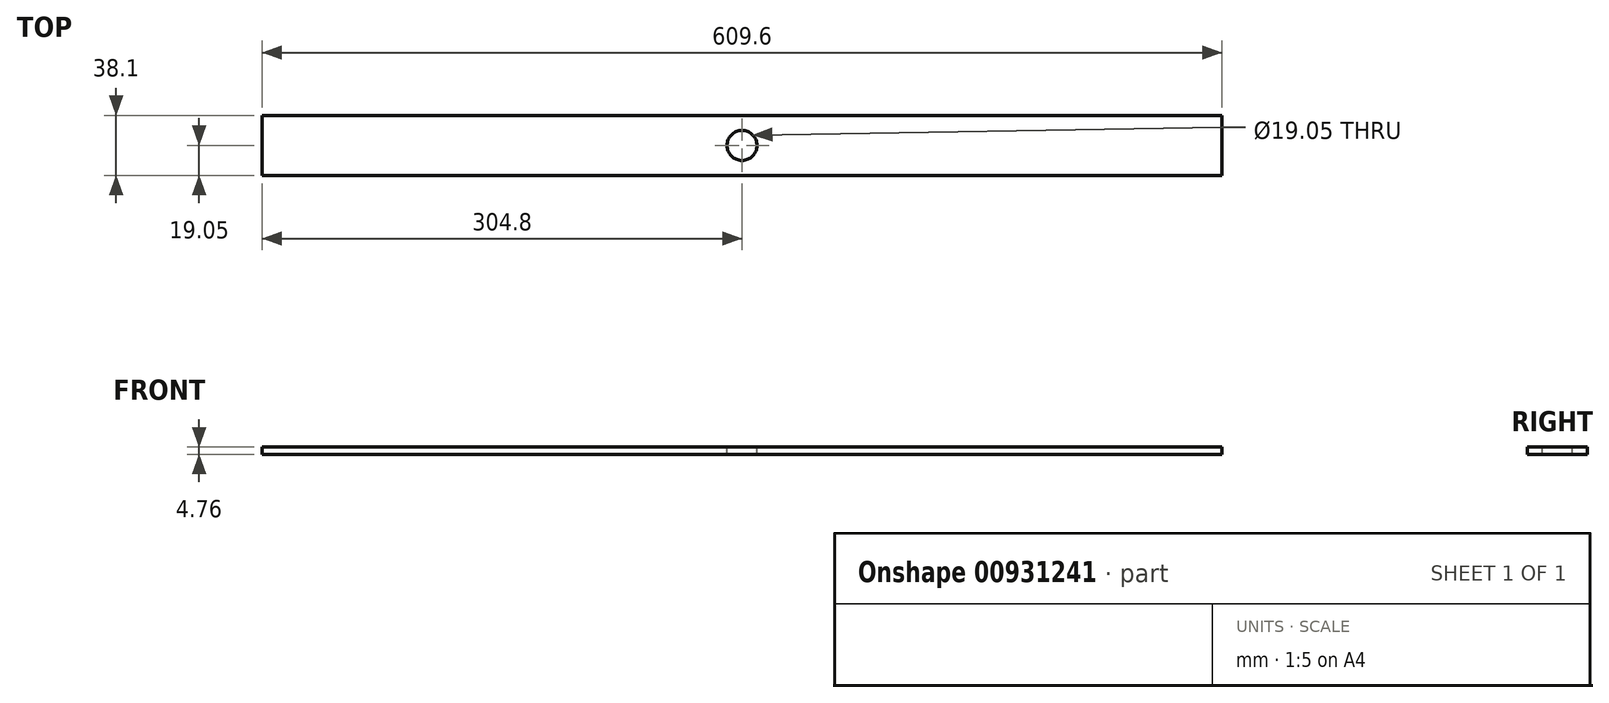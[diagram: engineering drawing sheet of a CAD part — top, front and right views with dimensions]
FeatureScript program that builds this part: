
annotation { "Feature Type Name" : "Feature", "Feature Type Description" : "" }
export const myFeature = defineFeature(function(context is Context, id is Id, definition is map)
    precondition{}
    {
        {
            var Q0;
            Q0=qCreatedBy(makeId("Right.planeOp"),FACE);
            var sketch = newSketch(context, id + "F0", { "sketchPlane" : qUnion([Q0])});
            skLineSegment(sketch, "E0.bottom", {"start": v(0, 0) * mm, "end": v(38.1, 0) * mm});
            skLineSegment(sketch, "E0.top", {"start": v(0, 4.76) * mm, "end": v(38.1, 4.76) * mm});
            skLineSegment(sketch, "E0.left", {"start": v(0, 0) * mm, "end": v(0, 4.76) * mm});
            skLineSegment(sketch, "E0.right", {"start": v(38.1, 0) * mm, "end": v(38.1, 4.76) * mm});
            skSolve(sketch);
        }
        {
            var Q0;
            Q0 = qSketchRegion(id + "F0", true);
            extrude(context, id + "F1", {"entities" : qUnion([Q0]), "depth" : 609.6 * mm, "offsetDistance" : 25.4 * mm});
        }
        {
            var Q0;
            Q0=makeQuery(id+"F1.opExtrude","SWEPT_FACE",FACE,{"disambiguationData":[OSD([sQuery(id+"F0.wireOp",EDGE,"E0.top")])]});
            var sketch = newSketch(context, id + "F2", { "sketchPlane" : qUnion([Q0])});
            skCircle(sketch, "E1", {"center": v(304.8, 19.05) * mm, "radius": 9.53 * mm});
            skPoint(sketch, "E1.centerSnap0", {"position": v(304.8, 38.1) * mm});
            skPoint(sketch, "E1.centerSnap1", {"position": v(0, 19.05) * mm});
            skSolve(sketch);
        }
        {
            var Q0;
            Q0 = qSketchRegion(id + "F2", true);
            extrude(context, id + "F3", {"entities" : qUnion([Q0]), "operationType" : NewBodyOperationType.REMOVE, "oppositeDirection" : true, "depth" : 25.4 * mm, "offsetDistance" : 25.4 * mm});
        }
    });
